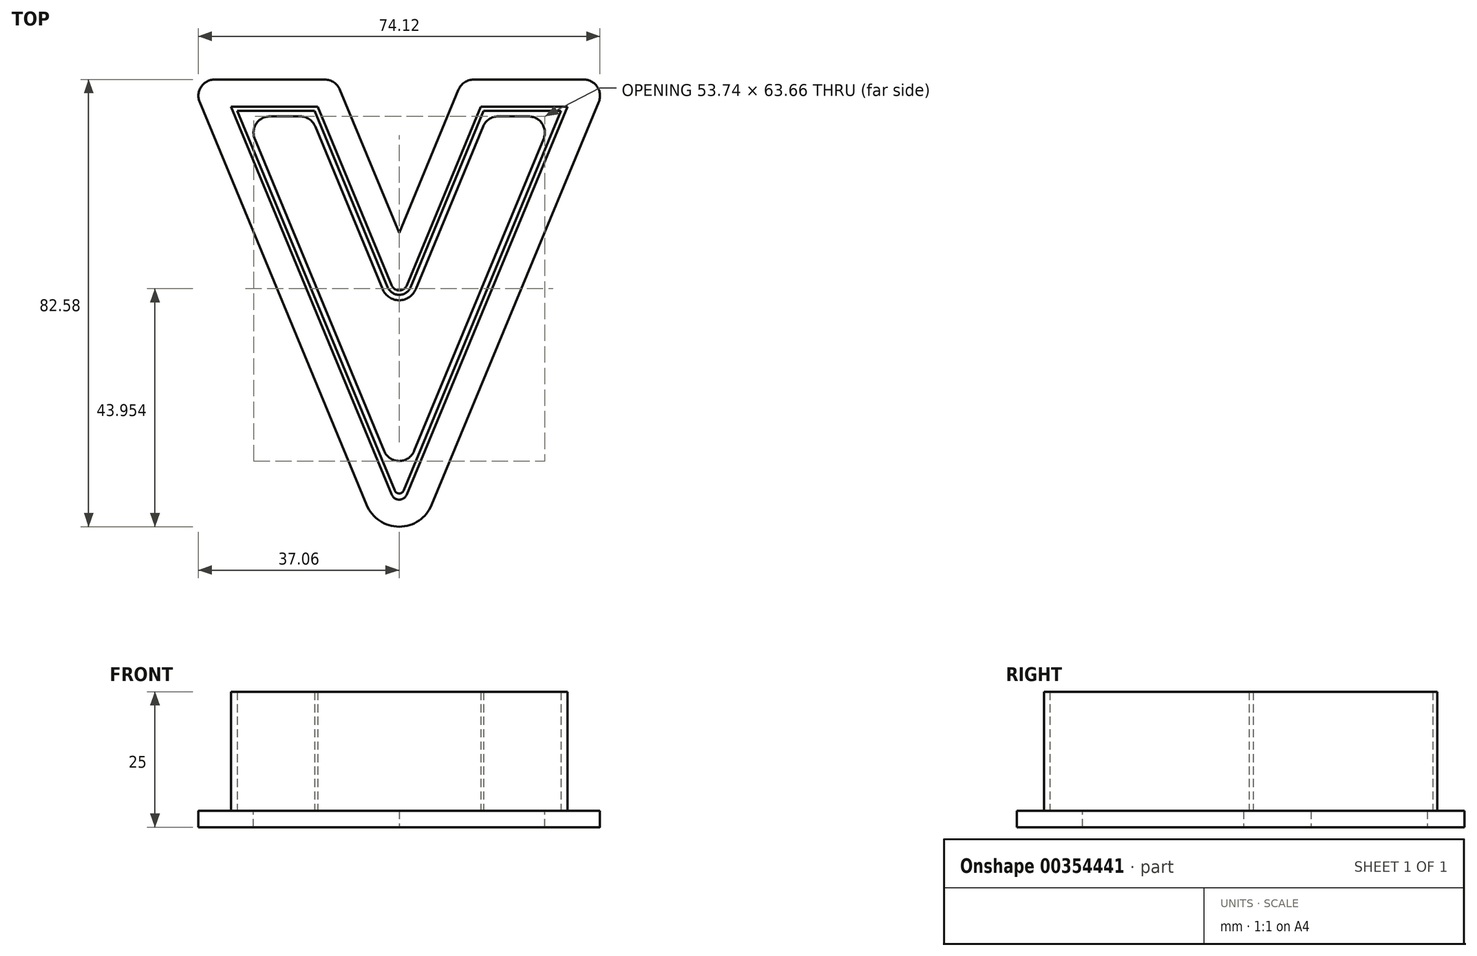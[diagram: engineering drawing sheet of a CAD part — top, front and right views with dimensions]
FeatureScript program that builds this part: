
annotation { "Feature Type Name" : "Feature", "Feature Type Description" : "" }
export const myFeature = defineFeature(function(context is Context, id is Id, definition is map)
    precondition{}
    {
        {
            var Q0;
            Q0=qCreatedBy(makeId("Top.planeOp"),FACE);
            var sketch = newSketch(context, id + "F0", { "sketchPlane" : qUnion([Q0])});
            skLineSegment(sketch, "E0", {"start": v(-15.07, 36.37) * mm, "end": v(-1.39, 3.35) * mm});
            skLineSegment(sketch, "E1", {"start": v(1.39, 3.35) * mm, "end": v(15.07, 36.37) * mm});
            skLineSegment(sketch, "E2", {"start": v(15.07, 36.37) * mm, "end": v(-15.07, 36.37) * mm});
            skLineSegment(sketch, "E3", {"start": v(0, 0) * mm, "end": v(0, 36.37) * mm, "construction": true});
            skLineSegment(sketch, "E4", {"start": v(15.07, 36.37) * mm, "end": v(31.07, 36.37) * mm});
            skLineSegment(sketch, "E5", {"start": v(31.07, 36.37) * mm, "end": v(1.39, -35.28) * mm});
            skLineSegment(sketch, "E6", {"start": v(-1.39, -35.28) * mm, "end": v(-31.07, 36.37) * mm});
            skLineSegment(sketch, "E7", {"start": v(-31.07, 36.37) * mm, "end": v(-15.07, 36.37) * mm});
            skPoint(sketch, "E8.visualSharp", {"position": v(0, 0) * mm});
            skArc(sketch, "E8.filletArc", {"start": v(-1.39, 3.35) * mm, "mid": v(0, 2.42) * mm, "end": v(1.39, 3.35) * mm});
            skPoint(sketch, "E9.visualSharp", {"position": v(0, -38.63) * mm});
            skArc(sketch, "E9.filletArc", {"start": v(-1.39, -35.28) * mm, "mid": v(0, -36.2) * mm, "end": v(1.39, -35.28) * mm});
            skLineSegment(sketch, "E10.0", {"start": v(-0.83, -34.53) * mm, "end": v(-29.87, 35.57) * mm});
            skLineSegment(sketch, "E10.1", {"start": v(29.87, 35.57) * mm, "end": v(0.83, -34.53) * mm});
            skLineSegment(sketch, "E10.2", {"start": v(-15.6, 35.57) * mm, "end": v(-2.12, 3.04) * mm});
            skArc(sketch, "E10.3", {"start": v(-2.12, 3.04) * mm, "mid": v(0, 1.62) * mm, "end": v(2.12, 3.04) * mm});
            skLineSegment(sketch, "E10.4", {"start": v(2.12, 3.04) * mm, "end": v(15.6, 35.57) * mm});
            skLineSegment(sketch, "E10.5", {"start": v(-29.87, 35.57) * mm, "end": v(-15.6, 35.57) * mm});
            skLineSegment(sketch, "E10.6", {"start": v(15.6, 35.57) * mm, "end": v(29.87, 35.57) * mm});
            skLineSegment(sketch, "E11.0", {"start": v(0, -33.92) * mm, "end": v(-28.37, 34.57) * mm});
            skLineSegment(sketch, "E11.1", {"start": v(28.37, 34.57) * mm, "end": v(0, -33.92) * mm});
            skLineSegment(sketch, "E11.2", {"start": v(-16.27, 34.57) * mm, "end": v(-3.05, 2.66) * mm});
            skArc(sketch, "E11.3", {"start": v(-3.05, 2.66) * mm, "mid": v(0, 0.62) * mm, "end": v(3.05, 2.66) * mm});
            skLineSegment(sketch, "E11.4", {"start": v(3.05, 2.66) * mm, "end": v(16.27, 34.57) * mm});
            skLineSegment(sketch, "E11.5", {"start": v(-28.37, 34.57) * mm, "end": v(-16.27, 34.57) * mm});
            skLineSegment(sketch, "E11.6", {"start": v(16.27, 34.57) * mm, "end": v(28.37, 34.57) * mm});
            skPoint(sketch, "E12.visualSharp", {"position": v(0, -36.54) * mm});
            skArc(sketch, "E12.filletArc", {"start": v(-0.83, -34.53) * mm, "mid": v(0, -35.09) * mm, "end": v(0.83, -34.53) * mm});
            skLineSegment(sketch, "E13.0", {"start": v(-38.55, 41.37) * mm, "end": v(-11.73, 41.37) * mm});
            skLineSegment(sketch, "E13.1", {"start": v(-6, -37.2) * mm, "end": v(-38.55, 41.37) * mm});
            skLineSegment(sketch, "E13.2", {"start": v(0, 13.07) * mm, "end": v(11.73, 41.37) * mm});
            skLineSegment(sketch, "E13.3", {"start": v(11.73, 41.37) * mm, "end": v(38.55, 41.37) * mm});
            skLineSegment(sketch, "E13.4", {"start": v(38.55, 41.37) * mm, "end": v(6, -37.2) * mm});
            skLineSegment(sketch, "E13.5", {"start": v(-11.73, 41.37) * mm, "end": v(0, 13.07) * mm});
            skArc(sketch, "E13.6", {"start": v(-6, -37.2) * mm, "mid": v(0, -41.2) * mm, "end": v(6, -37.2) * mm});
            skSolve(sketch);
        }
        {
            var Q0;
            {var subQ5=sQuery(id+"F0.wireOp",EDGE,"E4");Q0=makeQuery(id+"F0.imprint","IMPRINT",FACE,{"disambiguationData":[TD([[makeQuery(id+"F0.imprint","IMPRINT",EDGE,{"derivedFrom":subQ5}),1.0]])]});}
            var Q1;
            Q1=makeQuery(id+"F0.imprint","IMPRINT",FACE,{"disambiguationData":[TD([[makeQuery(id+"F0.imprint","IMPRINT",EDGE,{"derivedFrom":sQuery(id+"F0.wireOp",EDGE,"E10.0")}),-1.0]])]});
            var Q2;
            {var subQ1=sQuery(id+"F0.wireOp",EDGE,"E0");Q2=makeQuery(id+"F0.imprint","IMPRINT",FACE,{"disambiguationData":[TD([[makeQuery(id+"F0.imprint","IMPRINT",EDGE,{"derivedFrom":subQ1}),1.0]])]});}
            var Q3;
            Q3=makeQuery(id+"F0.imprint","IMPRINT",FACE,{"disambiguationData":[TD([[makeQuery(id+"F0.imprint","IMPRINT",EDGE,{"derivedFrom":sQuery(id+"F0.wireOp",EDGE,"E0")}),-1.0]])]});
            extrude(context, id + "F1", {"entities" : qUnion([Q0, Q1, Q2, Q3]), "depth" : 3 * mm});
        }
        {
            var Q0;
            Q0=makeQuery(id+"F0.imprint","IMPRINT",FACE,{"disambiguationData":[TD([[makeQuery(id+"F0.imprint","IMPRINT",EDGE,{"derivedFrom":sQuery(id+"F0.wireOp",EDGE,"E0")}),-1.0]])]});
            extrude(context, id + "F2", {"entities" : qUnion([Q0]), "operationType" : NewBodyOperationType.ADD, "depth" : 25 * mm});
        }
        {
            var Q0;
            Q0=makeQuery(id+"F1.opExtrude","SWEPT_EDGE",EDGE,{"disambiguationData":[OSD([sQuery(id+"F0.wireOp",EDGE,"E13.0"),sQuery(id+"F0.wireOp",EDGE,"E13.1")])]});
            var Q1;
            Q1=makeQuery(id+"F1.opExtrude","SWEPT_EDGE",EDGE,{"disambiguationData":[OSD([sQuery(id+"F0.wireOp",EDGE,"E13.0"),sQuery(id+"F0.wireOp",EDGE,"E13.5")])]});
            var Q2;
            Q2=makeQuery(id+"F1.opExtrude","SWEPT_EDGE",EDGE,{"disambiguationData":[OSD([sQuery(id+"F0.wireOp",EDGE,"E13.2"),sQuery(id+"F0.wireOp",EDGE,"E13.3")])]});
            var Q3;
            Q3=makeQuery(id+"F1.opExtrude","SWEPT_EDGE",EDGE,{"disambiguationData":[OSD([sQuery(id+"F0.wireOp",EDGE,"E13.3"),sQuery(id+"F0.wireOp",EDGE,"E13.4")])]});
            var Q4;
            Q4=makeQuery(id+"F1.opExtrude","SWEPT_EDGE",EDGE,{"disambiguationData":[OSD([sQuery(id+"F0.wireOp",EDGE,"E11.2"),sQuery(id+"F0.wireOp",EDGE,"E11.5")])]});
            var Q5;
            Q5=makeQuery(id+"F1.opExtrude","SWEPT_EDGE",EDGE,{"disambiguationData":[OSD([sQuery(id+"F0.wireOp",EDGE,"E11.0"),sQuery(id+"F0.wireOp",EDGE,"E11.5")])]});
            var Q6;
            Q6=makeQuery(id+"F1.opExtrude","SWEPT_EDGE",EDGE,{"disambiguationData":[OSD([sQuery(id+"F0.wireOp",EDGE,"E11.4"),sQuery(id+"F0.wireOp",EDGE,"E11.6")])]});
            var Q7;
            Q7=makeQuery(id+"F1.opExtrude","SWEPT_EDGE",EDGE,{"disambiguationData":[OSD([sQuery(id+"F0.wireOp",EDGE,"E11.1"),sQuery(id+"F0.wireOp",EDGE,"E11.6")])]});
            var Q8;
            Q8=makeQuery(id+"F1.opExtrude","SWEPT_EDGE",EDGE,{"disambiguationData":[OSD([sQuery(id+"F0.wireOp",EDGE,"E11.0"),sQuery(id+"F0.wireOp",EDGE,"E11.1")])]});
            fillet(context, id + "F3", {"entities" : qUnion([Q0, Q1, Q2, Q3, Q4, Q5, Q6, Q7, Q8]), "radius" : 3 * mm, "tangentPropagation" : true, "allowEdgeOverflow" : false});
        }
    });
